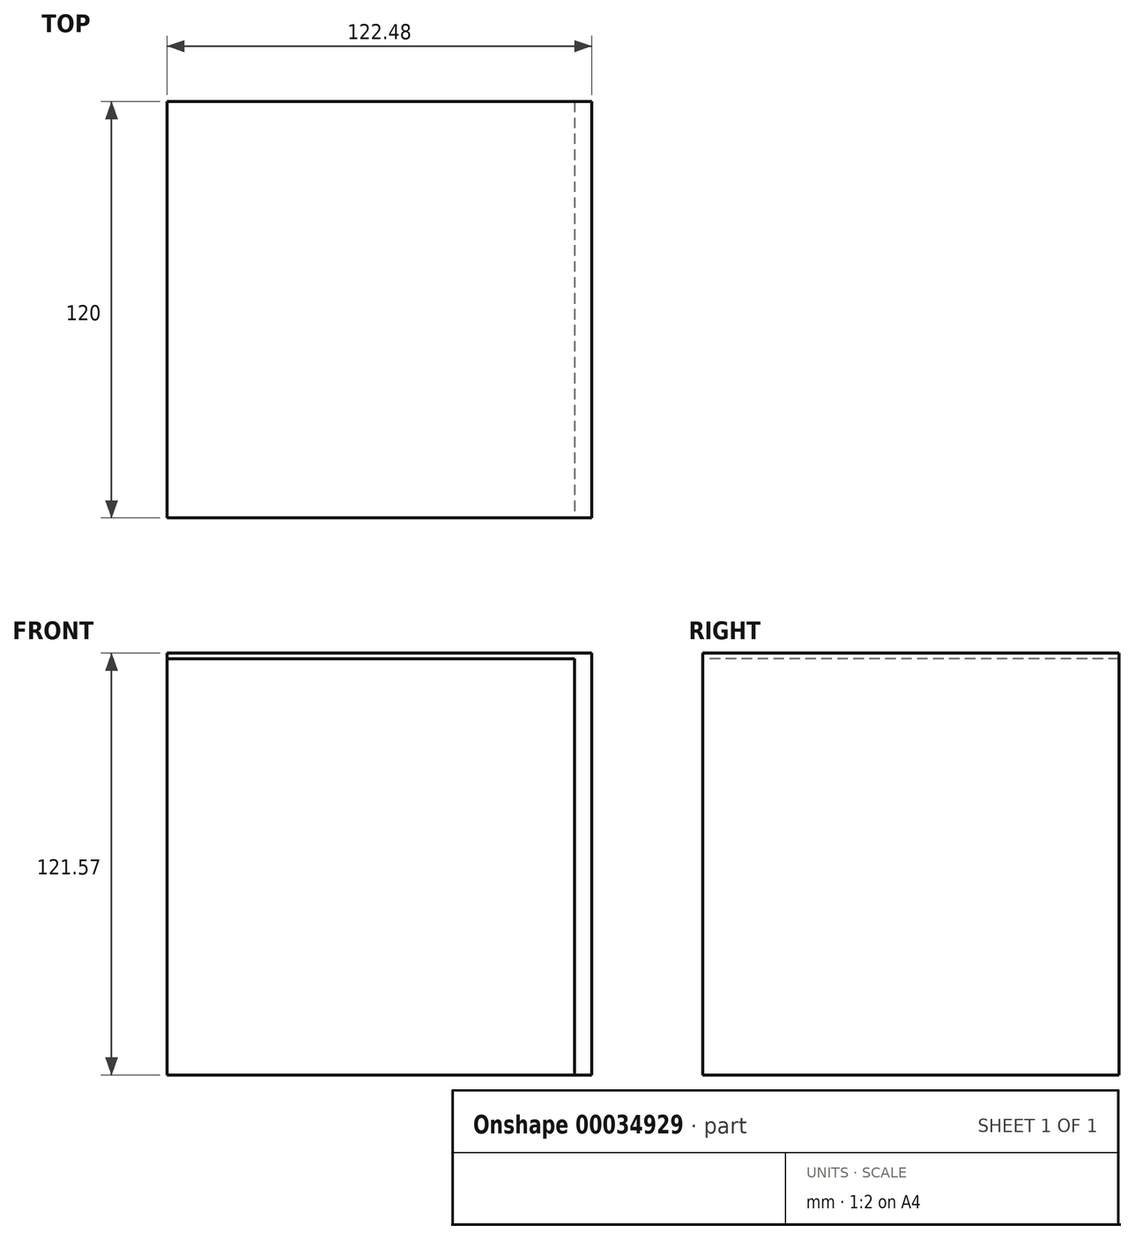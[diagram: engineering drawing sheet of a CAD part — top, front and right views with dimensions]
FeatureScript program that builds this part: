
annotation { "Feature Type Name" : "Feature", "Feature Type Description" : "" }
export const myFeature = defineFeature(function(context is Context, id is Id, definition is map)
    precondition{}
    {
        {
            var Q0;
            Q0=qCreatedBy(makeId("Front.planeOp"),FACE);
            var sketch = newSketch(context, id + "F0", { "sketchPlane" : qUnion([Q0])});
            skLineSegment(sketch, "E0.bottom", {"start": v(-59.18, 59.52) * mm, "end": v(63.3, 59.52) * mm});
            skLineSegment(sketch, "E0.top", {"start": v(-59.18, -62.05) * mm, "end": v(63.3, -62.05) * mm});
            skLineSegment(sketch, "E0.left", {"start": v(-59.18, 59.52) * mm, "end": v(-59.18, -62.05) * mm});
            skLineSegment(sketch, "E0.right", {"start": v(63.3, 59.52) * mm, "end": v(63.3, -62.05) * mm});
            skSolve(sketch);
        }
        {
            var Q0;
            Q0=sQuery(id+"F0.wireOp",EDGE,"E0.bottom");
            var Q1;
            Q1=sQuery(id+"F0.wireOp",EDGE,"E0.left");
            var Q2;
            Q2=sQuery(id+"F0.wireOp",EDGE,"E0.right");
            var Q3;
            Q3=sQuery(id+"F0.wireOp",EDGE,"E0.top");
            extrude(context, id + "F1", {"bodyType" : ToolBodyType.SURFACE, "surfaceEntities" : qUnion([Q0, Q1, Q2, Q3]), "depth" : 120 * mm});
        }
        {
            var Q0;
            Q0=makeQuery(id+"F1.opExtrude","SWEPT_EDGE",EDGE,{"disambiguationData":[OSD([sQuery(id+"F0.wireOp",VERTEX,"E0.right.start")])]});
            var Q1;
            Q1=makeQuery(id+"F1.opExtrude","SWEPT_EDGE",EDGE,{"disambiguationData":[OSD([sQuery(id+"F0.wireOp",VERTEX,"E0.top.end")])]});
            var Q2;
            Q2=makeQuery(id+"F1.opExtrude","SWEPT_EDGE",EDGE,{"disambiguationData":[OSD([sQuery(id+"F0.wireOp",VERTEX,"E0.left.start")])]});
            fillet(context, id + "F2", {"entities" : qUnion([Q0, Q1, Q2]), "radius" : 5 * mm, "tangentPropagation" : true, "allowEdgeOverflow" : false});
        }
        {
            var Q0;
            Q0=makeQuery(id+"F0.imprint","IMPRINT",FACE,{"disambiguationData":[TD([[makeQuery(id+"F0.imprint","IMPRINT",EDGE,{"derivedFrom":sQuery(id+"F0.wireOp",EDGE,"E0.bottom")}),-1.0]])]});
            extrude(context, id + "F3", {"entities" : qUnion([Q0]), "depth" : 120 * mm});
        }
        {
            var Q0;
            Q0=makeQuery(id+"F1.opExtrude","SWEPT_FACE",FACE,{"disambiguationData":[OSD([sQuery(id+"F0.wireOp",EDGE,"E0.top")])]});
            extrude(context, id + "F4", {"entities" : qUnion([Q0]), "depth" : 120 * mm});
        }
    });
